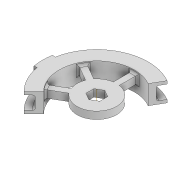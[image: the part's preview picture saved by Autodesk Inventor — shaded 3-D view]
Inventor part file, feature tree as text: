
AUTODESK INVENTOR PART (.ipt)
format: ipt  version: 2022 (Build 260153000, 153)  size: 257,536 bytes
history: native  units: mm
features: extrude x9, sketch x8, projected_geometry x5, fillet x2
ambient origin geometry x8: Origin, YZ Plane, XZ Plane, XY Plane, X Axis, Y Axis, Z Axis, Center Point
bodies: Solid1 (feature_tree)
feature tree (24):
  extrude  "Extrusion1"  Depth=44.0mm
  extrude  "Extrusion4"  Depth=3.7mm
  extrude  "Extrusion10"  Depth=1.5mm TaperAngle=0.0deg
  extrude  "Extrusion5"  Depth=3.0mm
  extrude  "Extrusion7"  Depth=1.5mm
  extrude  "Extrusion8"  Depth=10.0mm TaperAngle=0.0deg
  fillet  "Fillet1"  Radius=7.0mm
  extrude  "Extrusion9"  Depth=1.0mm
  fillet  "Fillet2"  [1 undecoded]
  sketch  "Sketch12"  dims[d35=45.0deg d36=10.0mm d37=0.0mm d38=3.0mm d39=3.0mm d40=0.0mm d41=20.0mm d42=1.0mm d43=1.5mm d45=9.7mm d46=0.0mm d47=10.0mm d48=0.0mm d49=3.490659mm d50=1.745329mm]
  extrude  "Extrusion11"  Depth=10.0mm TaperAngle=0.0deg
  extrude  "Extrusion12"  Depth=3.0mm
  sketch  "Sketch1"  dims[d0=4.1mm d1=44.0mm]
  sketch  "Sketch5"  dims[d2=3.7mm d3=0.0mm d11=4.0mm]
  projected_geometry  "Projected Loop4"
  sketch  "Sketch6"  dims[d12=1.5mm d13=0.0mm d15=1.5mm d16=0.0mm]
  projected_geometry  "Projected Loop5"
  sketch  "Sketch7"  dims[d17=3.0mm d19=20.0mm]
  projected_geometry  "Projected Loop6"
  sketch  "Sketch8"  dims[d20=3.0mm d21=1.5mm]
  sketch  "Sketch9"  dims[d24=60.0mm d26=360.0deg d28=10.0mm d29=0.0mm d30=7.0mm]
  sketch  "Sketch11"  dims[d31=10.0mm d32=0.0mm d33=1.0mm d34=150.0deg]
  projected_geometry  "Projected Loop7"
  projected_geometry  "Project Cut Edges1"
note: 1 required parameter value undecoded (feature->parameter linkage not recoverable at this tier; creation-order binding heuristic only, values carry confidence <= 0.55)
